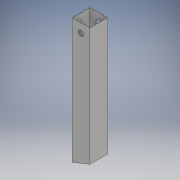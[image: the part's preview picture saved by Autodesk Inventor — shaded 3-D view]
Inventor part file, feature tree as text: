
AUTODESK INVENTOR PART (.ipt)
format: ipt  version: 2018 (Build 220112000, 112)  size: 118,272 bytes
history: native  units: mm
features: sketch x5, extrude x2, other x1, hole x1
ambient origin geometry x8: Origin, YZ Plane, XZ Plane, XY Plane, X Axis, Y Axis, Z Axis, Center Point
bodies: Body1 (feature_tree)
feature tree (9):
  other  "ソリッド1"
  sketch  "スケッチ1"
  extrude  "押し出し1"  Depth=32.0mm
  hole  "穴1"  [1 undecoded]
  sketch  "スケッチ4"
  extrude  "押し出し2"  Depth=30.4mm
  sketch  "スケッチ2"
  sketch  "スケッチ3"
  sketch  "スケッチ5"
note: 1 required parameter value undecoded (feature->parameter linkage not recoverable at this tier; creation-order binding heuristic only, values carry confidence <= 0.55)
